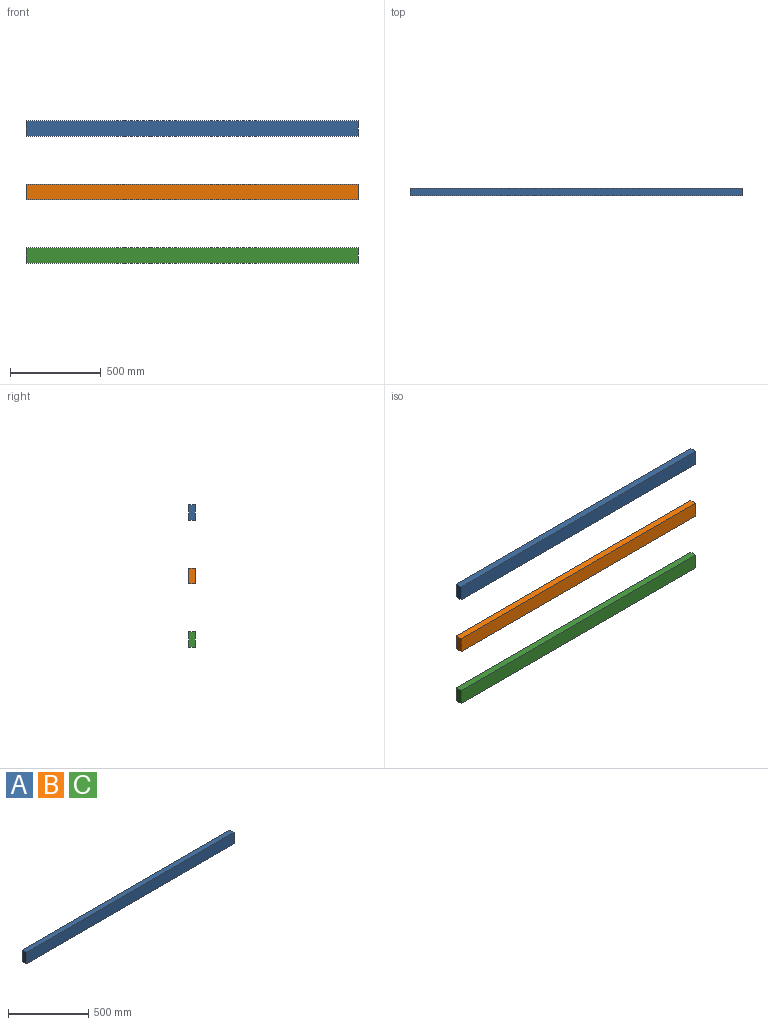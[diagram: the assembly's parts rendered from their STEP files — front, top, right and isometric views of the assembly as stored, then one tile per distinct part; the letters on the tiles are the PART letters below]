
ASSEMBLY  parts=3 mates=2
PART A: 6 faces, bbox 1830x38x87 mm
  f0: plane 1830x38mm, normal (0,0,1), area 69540mm2, adj f1,f3,f4,f5
  f1: plane 1830x87mm, normal (0,-1,0), area 159210mm2, adj f0,f2,f4,f5
  f2: plane 1830x38mm, normal (0,0,-1), area 69540mm2, adj f1,f3,f4,f5
  f3: plane 1830x87mm, normal (0,1,0), area 159210mm2, adj f0,f2,f4,f5
  f4: plane 87x38mm, normal (1,0,0), area 3306mm2, adj f0,f1,f2,f3
  f5: plane 87x38mm, normal (-1,0,0), area 3306mm2, adj f0,f1,f2,f3
PART B: same geometry as A
PART C: same geometry as A
PLACE A t=(-234.31,326.78,616.74)mm
PLACE B t=(-234.31,326.78,266.74)mm
PLACE C t=(-234.31,326.78,-83.26)mm
MATE fastened A.f1 <-> B.f1  axis (0,-1,0) through (-234.31,334.38,684.08)mm
MATE fastened B.f1 <-> C.f1  axis (0,-1,0) through (-234.31,334.38,334.08)mm
